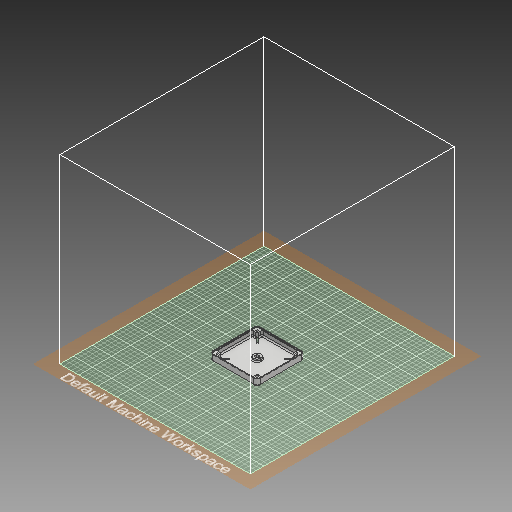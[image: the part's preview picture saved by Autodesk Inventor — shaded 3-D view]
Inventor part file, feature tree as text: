
AUTODESK INVENTOR PART (.ipt)
format: ipt  version: 2019 (Build 230136000, 136)  size: 735,744 bytes
history: native  units: mm
features: sketch x9, extrude x8, other x5, projected_geometry x4, fillet x3, reference x1
ambient origin geometry x8: Origin, YZ Plane, XZ Plane, XY Plane, X Axis, Y Axis, Z Axis, Center Point
bodies: Body1 (feature_tree)
feature tree (30):
  other  "Твердое тело1"
  extrude  "Выдавливание1"  Depth=2.5mm TaperAngle=0.0deg
  extrude  "Выдавливание2"  Depth=2.5mm
  other  "Выступ1"
  extrude  "Выдавливание3"  Depth=12.0mm TaperAngle=0.0deg
  fillet  "Сопряжение1"  Radius=6.0mm
  extrude  "Выдавливание4"  Depth=10.5mm
  fillet  "Сопряжение3"  Radius=6.0mm
  extrude  "Выдавливание5"  Depth=10.5mm
  sketch  "Эскиз6"
  extrude  "Выдавливание6"  Depth=6.0mm
  fillet  "Сопряжение4"  Radius=10.5mm
  extrude  "Выдавливание7"  Depth=10.0mm TaperAngle=0.0deg
  extrude  "Выдавливание8"  Depth=3.0mm
  sketch  "Эскиз1"
  sketch  "Эскиз2"
  projected_geometry  "Спроецированная петля1"
  sketch  "Эскиз3"
  projected_geometry  "Спроецированная петля2"
  sketch  "Эскиз4"
  sketch  "Эскиз5"
  reference  "Ссылка1"
  sketch  "Эскиз7"
  sketch  "Эскиз8"
  projected_geometry  "Спроецированная петля3"
  sketch  "Эскиз9"
  projected_geometry  "Спроецированная петля4"
  other  "<userpath>\Documents\GitHub\Tesla_coil_V1\3dModels\TeslaCoil.iam"
  other  "TeslaCoil.iam"
  other  "RackeSecondary:1"
